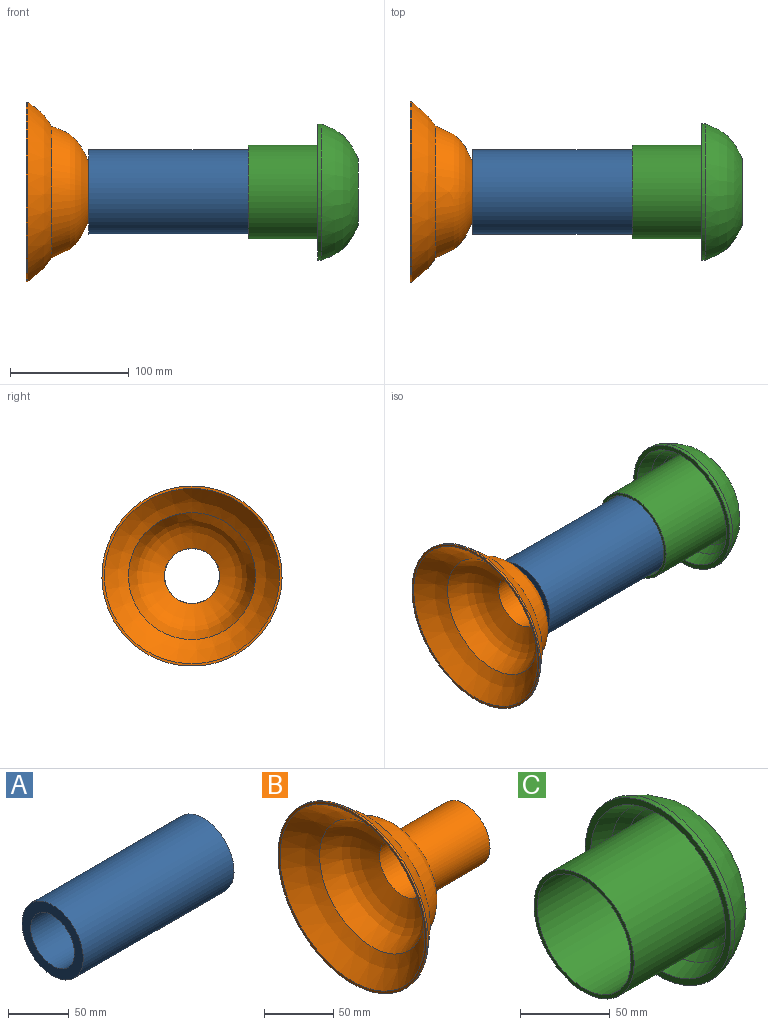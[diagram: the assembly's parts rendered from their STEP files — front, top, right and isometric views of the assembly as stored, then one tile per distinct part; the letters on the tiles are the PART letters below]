
ASSEMBLY  parts=3 mates=2
PART A: 4 faces, bbox 175.3x71.1x71.1 mm
  f0: cylinder r=25.4mm len=175.26mm, axis (-1,0,0), area 27970.3mm2, adj f1,f3
  f1: plane 71.12x71.12mm, normal (1,0,0), area 1945.8mm2, adj f0,f2
  f2: cylinder r=35.56mm len=175.26mm, axis (-1,0,0), area 39158.4mm2, adj f1,f3
  f3: plane 71.12x71.12mm, normal (-1,0,0), area 1945.8mm2, adj f0,f2
PART B: 9 faces, bbox 114.3x151.5x151.5 mm
  f0: revolved ~106.77x106.77mm, area 11632.9mm2, adj f1,f8
  f1: cylinder r=23.22mm len=63.5mm, axis (-1,0,0), area 9265.2mm2, adj f0,f2
  f2: plane 51.52x51.52mm, normal (1,0,0), area 390.9mm2, adj f1,f3
  f3: cylinder r=25.76mm len=61.84mm, axis (-1,0,0), area 10009.2mm2, adj f2,f4
  f4: revolved ~110.97x110.97mm, area 12156.9mm2, adj f3,f5
  f5: revolved ~151.53x151.53mm, area 11984.4mm2, adj f4,f6
  f6: cylinder r=75.76mm len=151.53mm, axis (-1,0,0), area 720.5mm2, adj f5,f7
  f7: plane 151.53x151.53mm, normal (-1,0,0), area 958mm2, adj f6,f8
  f8: revolved ~147.45x147.45mm, area 11601.8mm2, adj f0,f7
PART C: 12 faces, bbox 92.2x114.6x114.6 mm
  f0: revolved ~106.18x106.18mm, area 3986.4mm2, adj f1,f11
  f1: cone r=48.26mm half-angle=34.7deg, axis (-1,0,0), area 2565.2mm2, adj f0,f2
  f2: revolved ~86.36x86.36mm, area 1311.1mm2, adj f1,f3
  f3: cylinder r=39.37mm len=80.32mm, axis (1,0,0), area 19869.8mm2, adj f2,f4
  f4: plane 78.74x78.74mm, normal (-1,0,0), area 608mm2, adj f3,f5
  f5: cylinder r=36.83mm len=82.03mm, axis (1,0,0), area 18982.4mm2, adj f4,f6
  f6: revolved ~73.66x73.66mm, area 2903mm2, adj f5,f7
  f7: cylinder r=23.05mm len=46.1mm, axis (1,0,0), area 478.5mm2, adj f6,f8
  f8: plane 56.22x56.22mm, normal (1,0,0), area 813.2mm2, adj f7,f9
  f9: revolved ~114.56x114.56mm, area 12543.5mm2, adj f8,f10
  f10: cylinder r=57.28mm len=114.56mm, axis (1,0,0), area 1163mm2, adj f9,f11
  f11: plane 114.56x114.56mm, normal (-1,0,0), area 1452.5mm2, adj f0,f10
PLACE A t=(-9.8,-27.78,-83.76)mm
PLACE B t=(-139.39,-27.78,-83.76)mm
PLACE C t=(82.46,-27.78,-83.76)mm
MATE cylindrical C.f1 <-> A.f0  axis (1,0,0) through (37.92,-27.78,-83.76)mm
MATE cylindrical A.f0 <-> B.f1  axis (-1,0,0) through (-49.71,-27.78,-83.76)mm
